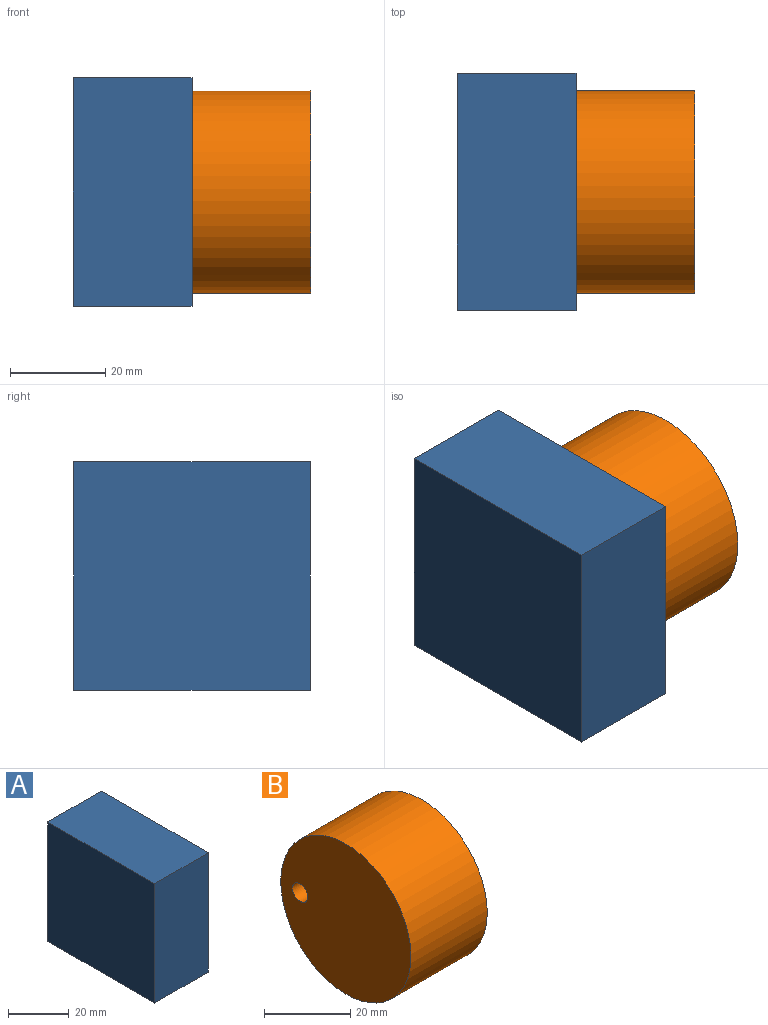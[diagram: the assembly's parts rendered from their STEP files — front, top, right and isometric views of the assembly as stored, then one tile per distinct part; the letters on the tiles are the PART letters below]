
ASSEMBLY  parts=2 mates=1
PART A: 6 faces, bbox 25x49.8x48.1 mm
  f0: plane 49.81x25mm, normal (0,0,-1), area 1245.2mm2, adj f1,f3,f4,f5
  f1: plane 48.09x25mm, normal (0,1,0), area 1202.3mm2, adj f0,f2,f4,f5
  f2: plane 49.81x25mm, normal (0,0,1), area 1245.2mm2, adj f1,f3,f4,f5
  f3: plane 48.09x25mm, normal (0,-1,0), area 1202.3mm2, adj f0,f2,f4,f5
  f4: plane 49.81x48.09mm, normal (1,0,0), area 2395.4mm2, adj f0,f1,f2,f3
  f5: plane 49.81x48.09mm, normal (-1,0,0), area 2395.4mm2, adj f0,f1,f2,f3
PART B: 4 faces, bbox 25x42.7x42.7 mm
  f0: cylinder r=21.33mm len=42.66mm, axis (-1,0,0), area 3350.8mm2, adj f1,f2
  f1: plane 42.66x42.66mm, normal (1,0,0), area 1409.9mm2, adj f0,f3
  f2: plane 42.66x42.66mm, normal (-1,0,0), area 1409.9mm2, adj f0,f3
  f3: cylinder r=2.5mm len=25mm, axis (1,0,0), area 392.7mm2, adj f1,f2
PLACE A t=(-19.44,66.26,-11.47)mm
PLACE B t=(5.56,-48.25,-26.64)mm
MATE revolute B.f0 <-> A.f4  axis (-1,0,0) through (5.56,6.29,15.44)mm
